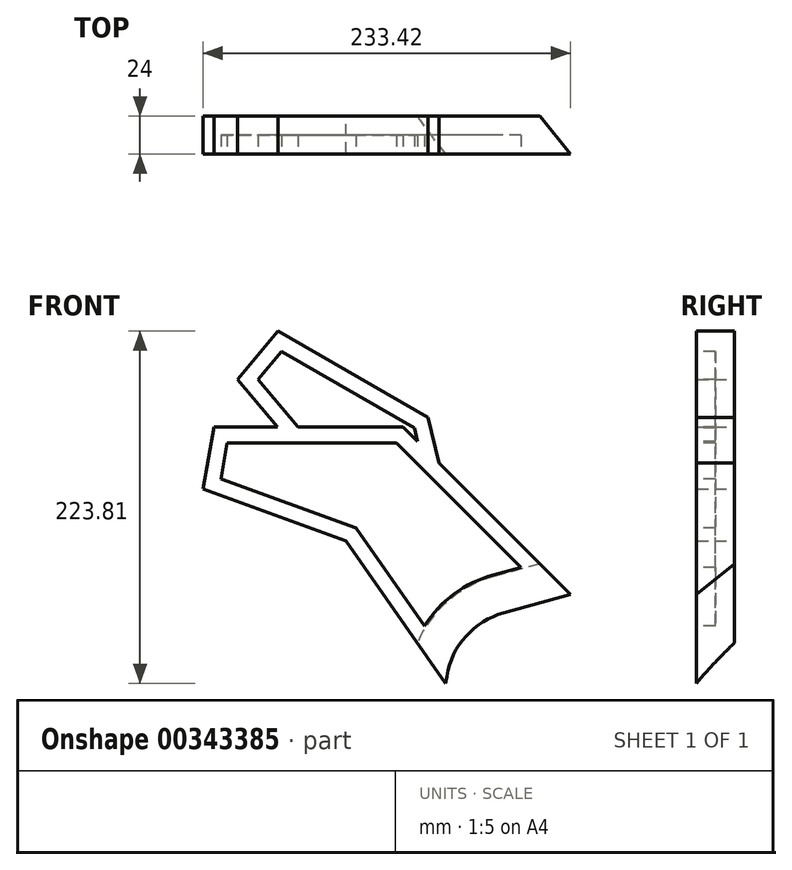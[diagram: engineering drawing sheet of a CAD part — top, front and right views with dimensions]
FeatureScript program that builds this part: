
annotation { "Feature Type Name" : "Feature", "Feature Type Description" : "" }
export const myFeature = defineFeature(function(context is Context, id is Id, definition is map)
    precondition{}
    {
        {
            var Q0;
            Q0=qCreatedBy(makeId("Front.planeOp"),FACE);
            var sketch = newSketch(context, id + "F0", { "sketchPlane" : qUnion([Q0])});
            skLineSegment(sketch, "E0", {"start": v(-42.13, -35.35) * mm, "end": v(42.13, 35.35) * mm, "construction": true});
            skLineSegment(sketch, "E1", {"start": v(0, 0) * mm, "end": v(-53.46, 0) * mm, "construction": true});
            skLineSegment(sketch, "E2", {"start": v(19.1, 62.8) * mm, "end": v(53.12, 22.26) * mm, "construction": true});
            skLineSegment(sketch, "E3", {"start": v(-7.55, 85.04) * mm, "end": v(-114.03, 191.51) * mm});
            skLineSegment(sketch, "E4", {"start": v(-86.96, 28.66) * mm, "end": v(-150.3, 119.11) * mm});
            skLineSegment(sketch, "E5", {"start": v(-114.03, 191.51) * mm, "end": v(-234.03, 191.51) * mm});
            skLineSegment(sketch, "E6", {"start": v(-234.03, 191.51) * mm, "end": v(-240.97, 152.12) * mm});
            skLineSegment(sketch, "E7", {"start": v(-240.97, 152.12) * mm, "end": v(-150.3, 119.11) * mm});
            skPoint(sketch, "E8.orphan", {"position": v(-168.8, 145.55) * mm});
            skLineSegment(sketch, "E9", {"start": v(-86.96, 28.66) * mm, "end": v(-0.72, 101.03) * mm, "construction": true});
            skLineSegment(sketch, "E10", {"start": v(-61.66, 39.64) * mm, "end": v(-7.55, 85.04) * mm, "construction": true});
            skLineSegment(sketch, "E11", {"start": v(-7.55, 85.04) * mm, "end": v(-81.06, 64.95) * mm});
            skLineSegment(sketch, "E12", {"start": v(-81.06, 64.95) * mm, "end": v(-86.96, 28.66) * mm});
            skPoint(sketch, "E13.visualSharp", {"position": v(-81.06, 64.95) * mm});
            skSolve(sketch);
        }
        {
            var Q0;
            Q0=makeQuery(id+"F0.imprint","IMPRINT",FACE,{"disambiguationData":[TD([[makeQuery(id+"F0.imprint","IMPRINT",EDGE,{"derivedFrom":sQuery(id+"F0.wireOp",EDGE,"E0")}),1.0]])]});
            var Q1;
            Q1=makeQuery(id+"F0.imprint","IMPRINT",FACE,{"disambiguationData":[TD([[makeQuery(id+"F0.imprint","IMPRINT",EDGE,{"derivedFrom":sQuery(id+"F0.wireOp",EDGE,"E3")}),1.0]])]});
            extrude(context, id + "F1", {"entities" : qUnion([Q0, Q1]), "depth" : 24 * mm});
        }
        {
            var Q0;
            Q0=makeQuery(id+"F1.opExtrude","SWEPT_EDGE",EDGE,{"disambiguationData":[OSD([sQuery(id+"F0.wireOp",EDGE,"E11"),sQuery(id+"F0.wireOp",EDGE,"E12")])]});
            fillet(context, id + "F2", {"entities" : qUnion([Q0]), "radius" : 50 * mm, "tangentPropagation" : true, "allowEdgeOverflow" : false});
        }
        {
            var Q0;
            Q0=makeQuery(id+"F1.opExtrude","CAP_EDGE",EDGE,{"disambiguationData":[OSD([sQuery(id+"F0.wireOp",EDGE,"E11")])],"isStart":true});
            chamfer(context, id + "F3", {"entities" : qUnion([Q0]), "chamferType" : ChamferType.TWO_OFFSETS, "width1" : 24 * mm, "oppositeDirection" : false, "width2" : 24 * mm, "tangentPropagation" : true});
        }
        {
            var Q0;
            Q0=makeQuery(id+"F1.opExtrude","CAP_FACE",FACE,{"disambiguationData":[OSD([sQuery(id+"F0.wireOp",EDGE,"E3"),sQuery(id+"F0.wireOp",EDGE,"E4"),sQuery(id+"F0.wireOp",EDGE,"E5"),sQuery(id+"F0.wireOp",EDGE,"E6"),sQuery(id+"F0.wireOp",EDGE,"E7"),sQuery(id+"F0.wireOp",EDGE,"E11"),sQuery(id+"F0.wireOp",EDGE,"E12")])],"isStart":false});
            cPlane(context, id + "F4", {"entities" : qUnion([Q0]), "cplaneType" : CPlaneType.OFFSET, "offset" : 12 * mm, "oppositeDirection" : true, "width" : 150 * mm, "height" : 150 * mm});
        }
        {
            var Q0;
            Q0=makeQuery(id+"F1.opExtrude","CAP_FACE",FACE,{"disambiguationData":[OSD([sQuery(id+"F0.wireOp",EDGE,"E3"),sQuery(id+"F0.wireOp",EDGE,"E4"),sQuery(id+"F0.wireOp",EDGE,"E5"),sQuery(id+"F0.wireOp",EDGE,"E6"),sQuery(id+"F0.wireOp",EDGE,"E7"),sQuery(id+"F0.wireOp",EDGE,"E11"),sQuery(id+"F0.wireOp",EDGE,"E12")])],"isStart":true});
            var sketch = newSketch(context, id + "F5", { "sketchPlane" : qUnion([Q0])});
            skLineSegment(sketch, "E14", {"start": v(163.59, 155.64) * mm, "end": v(219.13, 221.83) * mm});
            skLineSegment(sketch, "E15", {"start": v(219.13, 221.83) * mm, "end": v(193.42, 252.47) * mm});
            skLineSegment(sketch, "E16", {"start": v(193.42, 252.47) * mm, "end": v(98.15, 197.47) * mm});
            skLineSegment(sketch, "E17", {"start": v(98.15, 197.47) * mm, "end": v(84.04, 139.95) * mm});
            skLineSegment(sketch, "E18", {"start": v(84.04, 139.95) * mm, "end": v(163.59, 155.64) * mm});
            skSolve(sketch);
        }
        {
            var Q0;
            Q0 = qSketchRegion(id + "F5", true);
            extrude(context, id + "F6", {"entities" : qUnion([Q0]), "operationType" : NewBodyOperationType.ADD, "oppositeDirection" : true, "depth" : 12 * mm});
        }
        {
            var Q0;
            Q0=makeQuery(id+"F1.opExtrude","CAP_FACE",FACE,{"disambiguationData":[OSD([sQuery(id+"F0.wireOp",EDGE,"E3"),sQuery(id+"F0.wireOp",EDGE,"E4"),sQuery(id+"F0.wireOp",EDGE,"E5"),sQuery(id+"F0.wireOp",EDGE,"E6"),sQuery(id+"F0.wireOp",EDGE,"E7"),sQuery(id+"F0.wireOp",EDGE,"E11"),sQuery(id+"F0.wireOp",EDGE,"E12")])],"isStart":false});
            var sketch = newSketch(context, id + "F7", { "sketchPlane" : qUnion([Q0])});
            skLineSegment(sketch, "E19.0", {"start": v(-86.96, 28.66) * mm, "end": v(-150.3, 119.11) * mm, "construction": true});
            skLineSegment(sketch, "E20.0", {"start": v(-240.97, 152.12) * mm, "end": v(-150.3, 119.11) * mm, "construction": true});
            skLineSegment(sketch, "E21.0", {"start": v(-234.03, 191.51) * mm, "end": v(-240.97, 152.12) * mm, "construction": true});
            skLineSegment(sketch, "E22.0", {"start": v(-114.03, 191.51) * mm, "end": v(-234.03, 191.51) * mm, "construction": true});
            skLineSegment(sketch, "E23.0", {"start": v(-7.55, 85.04) * mm, "end": v(-114.03, 191.51) * mm, "construction": true});
            skLineSegment(sketch, "E24.0", {"start": v(-100.32, 65.18) * mm, "end": v(-143.9, 127.43) * mm});
            skLineSegment(sketch, "E24.1", {"start": v(-39.01, 102.36) * mm, "end": v(-118.17, 181.51) * mm});
            skLineSegment(sketch, "E24.2", {"start": v(-118.17, 181.51) * mm, "end": v(-225.63, 181.51) * mm});
            skLineSegment(sketch, "E24.3", {"start": v(-225.63, 181.51) * mm, "end": v(-229.67, 158.65) * mm});
            skLineSegment(sketch, "E24.4", {"start": v(-229.67, 158.65) * mm, "end": v(-143.9, 127.43) * mm});
            skArc(sketch, "E25.0", {"start": v(-100.32, 65.18) * mm, "mid": v(-81.51, 85.46) * mm, "end": v(-56.64, 97.54) * mm});
            skLineSegment(sketch, "E25.1", {"start": v(-39.01, 102.36) * mm, "end": v(-56.64, 97.54) * mm});
            skSolve(sketch);
        }
        {
            var Q0;
            Q0 = qSketchRegion(id + "F7", true);
            extrude(context, id + "F8", {"entities" : qUnion([Q0]), "operationType" : NewBodyOperationType.REMOVE, "oppositeDirection" : true, "depth" : 12 * mm});
        }
        {
            var Q0;
            Q0=makeQuery(id+"F6.opExtrude","CAP_FACE",FACE,{"disambiguationData":[OSD([sQuery(id+"F5.wireOp",EDGE,"E14"),sQuery(id+"F5.wireOp",EDGE,"E15"),sQuery(id+"F5.wireOp",EDGE,"E16"),sQuery(id+"F5.wireOp",EDGE,"E17"),sQuery(id+"F5.wireOp",EDGE,"E18")])],"isStart":false});
            extrude(context, id + "F9", {"entities" : qUnion([Q0]), "operationType" : NewBodyOperationType.ADD, "depth" : 12 * mm});
        }
        {
            var Q0;
            Q0=makeQuery(id+"F9.boolean.opBoolean","MERGE",FACE,{"derivedFrom":[makeQuery(id+"F1.opExtrude","CAP_FACE",FACE,{"disambiguationData":[OSD([sQuery(id+"F0.wireOp",EDGE,"E3"),sQuery(id+"F0.wireOp",EDGE,"E4"),sQuery(id+"F0.wireOp",EDGE,"E5"),sQuery(id+"F0.wireOp",EDGE,"E6"),sQuery(id+"F0.wireOp",EDGE,"E7"),sQuery(id+"F0.wireOp",EDGE,"E11"),sQuery(id+"F0.wireOp",EDGE,"E12")])],"isStart":false}),makeQuery(id+"F9.opExtrude","CAP_FACE",FACE,{"disambiguationData":[OSD([sQuery(id+"F5.wireOp",EDGE,"E14"),sQuery(id+"F5.wireOp",EDGE,"E15"),sQuery(id+"F5.wireOp",EDGE,"E16"),sQuery(id+"F5.wireOp",EDGE,"E17"),sQuery(id+"F5.wireOp",EDGE,"E18")])],"isStart":false})]});
            var sketch = newSketch(context, id + "F10", { "sketchPlane" : qUnion([Q0])});
            skLineSegment(sketch, "E26.0", {"start": v(-106.85, 190.94) * mm, "end": v(-104.7, 182.19) * mm});
            skLineSegment(sketch, "E26.1", {"start": v(-191.15, 239.61) * mm, "end": v(-106.85, 190.94) * mm});
            skLineSegment(sketch, "E26.2", {"start": v(-206.07, 221.83) * mm, "end": v(-191.15, 239.61) * mm});
            skLineSegment(sketch, "E26.3", {"start": v(-180.64, 191.51) * mm, "end": v(-206.07, 221.83) * mm});
            skLineSegment(sketch, "E27.0", {"start": v(-118.17, 181.51) * mm, "end": v(-225.63, 181.51) * mm, "construction": true});
            skLineSegment(sketch, "E28.0", {"start": v(-39.01, 102.36) * mm, "end": v(-118.17, 181.51) * mm, "construction": true});
            skLineSegment(sketch, "E29.0", {"start": v(-114.03, 191.51) * mm, "end": v(-180.64, 191.51) * mm});
            skLineSegment(sketch, "E30.0", {"start": v(-7.55, 85.04) * mm, "end": v(-91.06, 168.54) * mm, "construction": true});
            skPoint(sketch, "E31.orphan", {"position": v(-91.06, 168.54) * mm});
            skLineSegment(sketch, "E32.trimOffspring", {"start": v(-104.7, 182.19) * mm, "end": v(-114.03, 191.51) * mm});
            skSolve(sketch);
        }
        {
            var Q0;
            Q0=makeQuery(id+"F10.imprint","IMPRINT",FACE,{"disambiguationData":[TD([[makeQuery(id+"F10.imprint","IMPRINT",EDGE,{"derivedFrom":sQuery(id+"F10.wireOp",EDGE,"E26.0")}),-1.0]])]});
            extrude(context, id + "F11", {"entities" : qUnion([Q0]), "operationType" : NewBodyOperationType.REMOVE, "oppositeDirection" : true, "depth" : 12 * mm});
        }
    });
